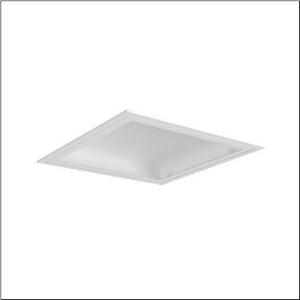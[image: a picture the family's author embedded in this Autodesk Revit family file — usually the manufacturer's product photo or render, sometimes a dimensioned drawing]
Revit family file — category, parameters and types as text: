
# Revit family: mira_r__21_51fr427a442a_c8f5
name_source: partatom
category: Lighting Fixtures
units: mm (PartAtom-declared; Revit-internal decimal feet)

## family parameters
Cut with Voids When Loaded = No
Host = Face
Light Source = No
Part Type = Normal
Room Calculation Point = No
Round Connector Dimension = Use Diameter
Shared = No

## types (1)
- Mira® 21 (1 x LED, 4860 lm, 37 W, 4000K)
    Apparent Load = 37 VA
    CIE Flux Codes = 50 81 97 100 100
    Color Rendering = 80
    Color Temperature = 4000K
    Default Elevation = 1800 mm
    Description = Mira® 21, clean room luminaire, primary light control with reflector, primary optical cover: cover, of PC, light emission: direct distribution, primary light characteristic: symmetric, installation type: recessed, LED, rated luminous flux: 4.860lm, luminous efficacy: 131lm/W, light colour: 840, colour temperature: 4000K, control gear: ECG, with terminal, 3-pole, max. 2.5mm², mains connection: 230V, AC, 50/60Hz, rated input power: 37W, luminaire housing, of sheet steel, coated, pure white, module: M625, length: 623mm, width: 623mm, height: 115mm, protection rating (complete): IP54, insulation class (complete): insulation class I (protective earthing), certification: CE, UKCA, permissible operating ambient temperature: -5..+40°C, standard: EN 50419, packaging unit: 1 piece
    Height = 0 mm  [stored 0 ft]
    Lamp = 1 x LED
    Lamp Light Flux = 4860 lm
    Lamp Power = 37 W
    Lamp count = 1
    Length = 625 mm
    Luminous efficacy = 131 lm/W
    Manufacturer = Siteco
    ModVariant = No
    Model = 51FR427A442A
    Mounting Place = Ceiling
    Mounting Type = Recessed
    Number of Poles = 1
    OnlyDefault = Yes
    Power Factor = 1
    Product Name = Mira® 21
    Product group = clean room luminaire
    ProductGroupID = 401
    Protection Class = Protection class I
    Protection Degree = IP 54
    RLX_Detail_Level = 1
    RlxData = <blob elided: 13313 chars, md5=bff44136>
    Socket = socket
    Standby Power = 0 W
    System Light Flux = 4860 lm
    System Power = 37 W
    Type Comments = Product without accessories
    Type Image = l_1007109.jpg
    URL = http://relux.com
    VarID = ---
    Voltage = 0 V
    Weight = 0.00 kg
    Width = 625 mm

note: [stored X ft] marks values corroborated as IEEE doubles in the binary element streams (Revit-internal decimal feet)

## geometry (parser evidence)
native form markers: Sweep x8
no freeform markers — native parametric forms only
